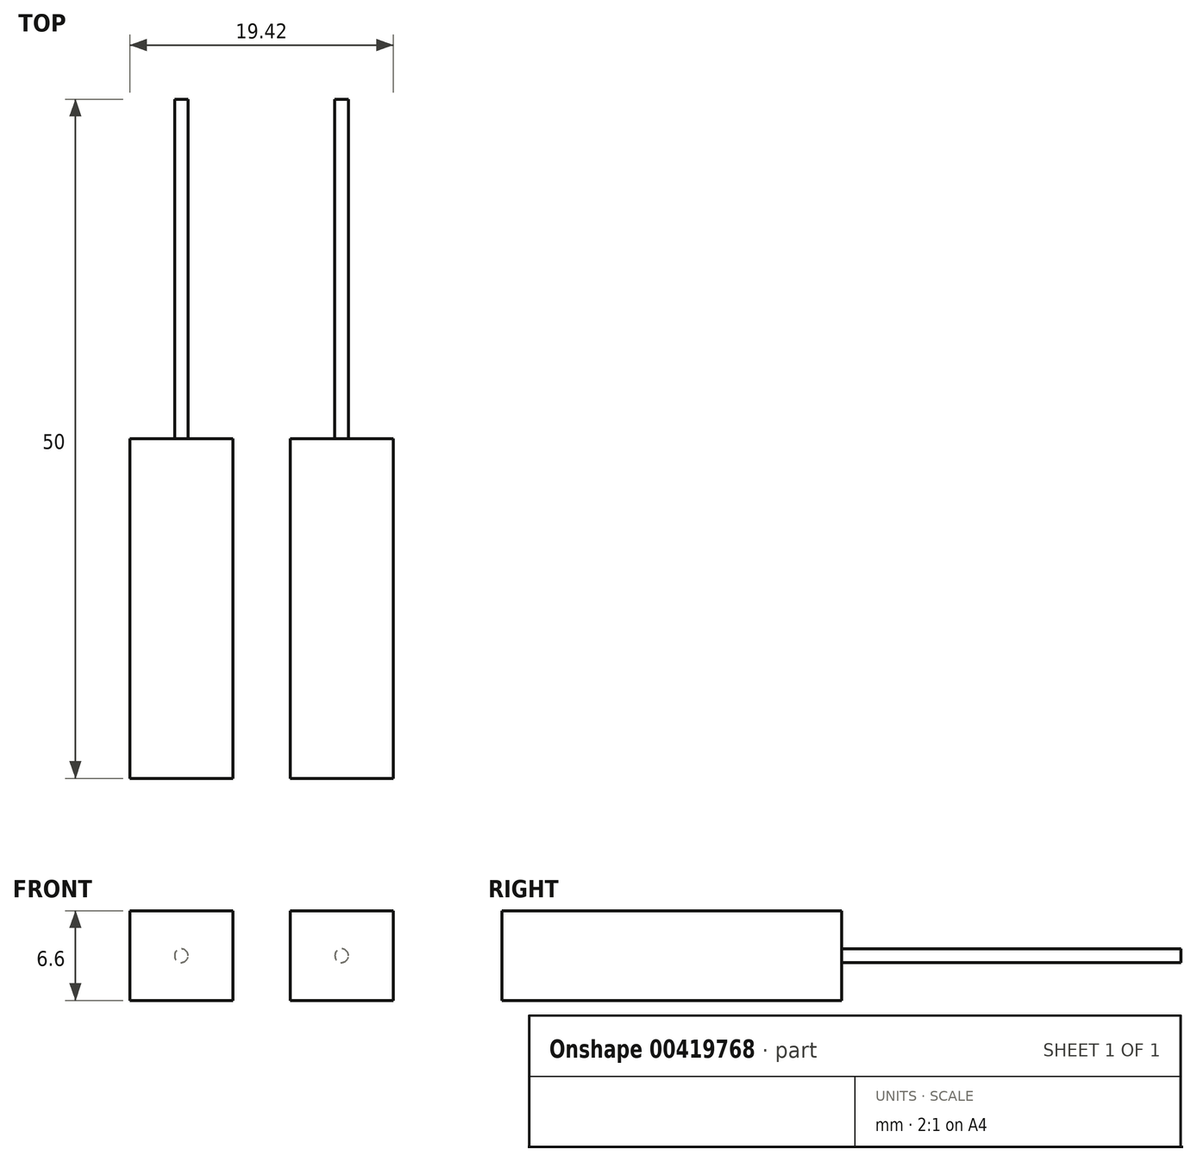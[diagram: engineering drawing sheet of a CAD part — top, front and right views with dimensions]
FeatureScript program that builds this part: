
annotation { "Feature Type Name" : "Feature", "Feature Type Description" : "" }
export const myFeature = defineFeature(function(context is Context, id is Id, definition is map)
    precondition{}
    {
        {
            var Q0;
            Q0=qCreatedBy(makeId("Front.planeOp"),FACE);
            var sketch = newSketch(context, id + "F0", { "sketchPlane" : qUnion([Q0])});
            skLineSegment(sketch, "E0.0", {"start": v(9.7, 3.3) * mm, "end": v(9.7, -3.3) * mm});
            skLineSegment(sketch, "E0.1", {"start": v(9.7, 3.3) * mm, "end": v(2.1, 3.3) * mm});
            skLineSegment(sketch, "E0.2", {"start": v(2.1, 3.3) * mm, "end": v(2.1, -3.3) * mm});
            skLineSegment(sketch, "E0.3", {"start": v(9.7, -3.3) * mm, "end": v(2.1, -3.3) * mm});
            skLineSegment(sketch, "E1.0", {"start": v(-9.7, 3.3) * mm, "end": v(-2.1, 3.3) * mm});
            skLineSegment(sketch, "E1.1", {"start": v(-9.7, 3.3) * mm, "end": v(-9.7, -3.3) * mm});
            skLineSegment(sketch, "E1.2", {"start": v(-9.7, -3.3) * mm, "end": v(-2.1, -3.3) * mm});
            skLineSegment(sketch, "E1.3", {"start": v(-2.1, 3.3) * mm, "end": v(-2.1, -3.3) * mm});
            skCircle(sketch, "E2", {"center": v(-5.9, 0) * mm, "radius": 0.5 * mm});
            skCircle(sketch, "E3", {"center": v(5.9, 0) * mm, "radius": 0.5 * mm});
            skSolve(sketch);
        }
        {
            var Q0;
            Q0=makeQuery(id+"F0.imprint","IMPRINT",FACE,{"disambiguationData":[TD([[makeQuery(id+"F0.imprint","IMPRINT",EDGE,{"derivedFrom":sQuery(id+"F0.wireOp",EDGE,"E3")}),1.0]])]});
            var Q1;
            Q1=makeQuery(id+"F0.imprint","IMPRINT",FACE,{"disambiguationData":[TD([[makeQuery(id+"F0.imprint","IMPRINT",EDGE,{"derivedFrom":sQuery(id+"F0.wireOp",EDGE,"E2")}),1.0]])]});
            extrude(context, id + "F1", {"entities" : qUnion([Q0, Q1]), "oppositeDirection" : true, "depth" : 50 * mm});
        }
        {
            var Q0;
            Q0=makeQuery(id+"F0.imprint","IMPRINT",FACE,{"disambiguationData":[TD([[makeQuery(id+"F0.imprint","IMPRINT",EDGE,{"derivedFrom":sQuery(id+"F0.wireOp",EDGE,"E0.0")}),-1.0]])]});
            var Q1;
            Q1=makeQuery(id+"F0.imprint","IMPRINT",FACE,{"disambiguationData":[TD([[makeQuery(id+"F0.imprint","IMPRINT",EDGE,{"derivedFrom":sQuery(id+"F0.wireOp",EDGE,"E1.0")}),-1.0]])]});
            extrude(context, id + "F2", {"entities" : qUnion([Q0, Q1]), "operationType" : NewBodyOperationType.ADD, "oppositeDirection" : true, "depth" : 25 * mm});
        }
    });
